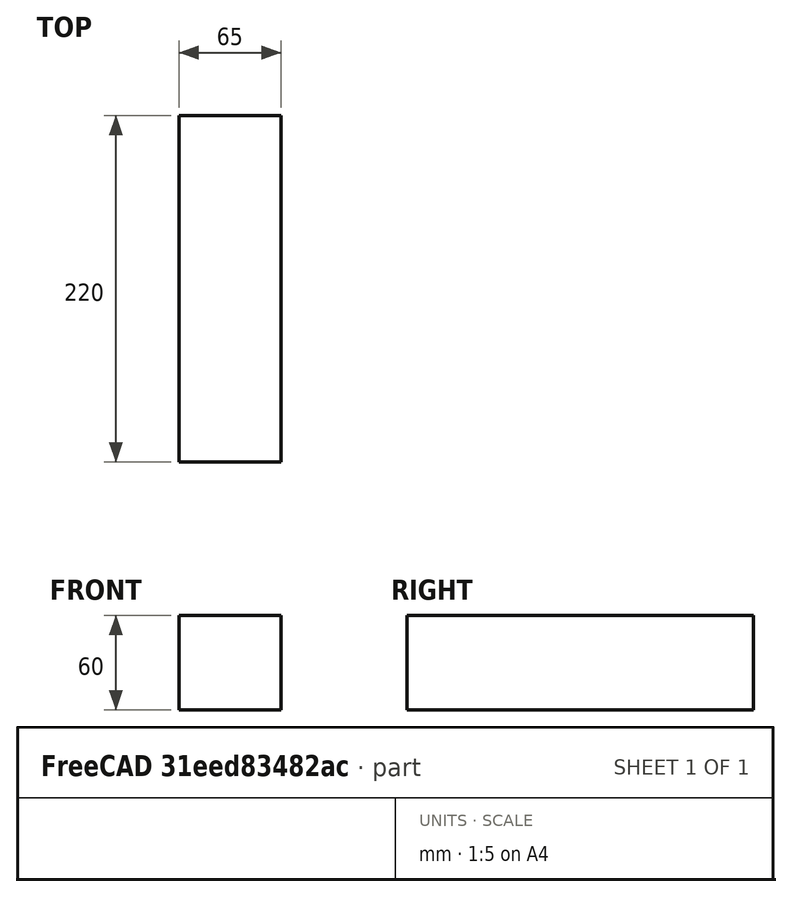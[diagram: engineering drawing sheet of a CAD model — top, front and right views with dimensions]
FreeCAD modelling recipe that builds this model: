
FCSTD DOCUMENT  (FreeCAD 0.15R4669 (Git))
Label: BR_batterie
License: All rights reserved
LicenseURL: http://en.wikipedia.org/wiki/All_rights_reserved
objects: Sketcher::SketchObject×1, Part::Extrusion×1
note: 2 computed .brp shape members not serialized (recipe doc carries the construction recipe); baked Part::Feature solids carry a one-line shape summary decoded from their .brp

FEATURE [Sketcher::SketchObject] Sketch  label="coupeBatt"
  Placement = pos=(0,0,0) rot=(-1,0,0;4.71239rad)
  sketch-geometry (4):
    g0: LineSegment StartX=-32.5 StartY=30 StartZ=0 EndX=32.5 EndY=30 EndZ=0
    g1: LineSegment StartX=32.5 StartY=30 StartZ=0 EndX=32.5 EndY=-30 EndZ=0
    g2: LineSegment StartX=32.5 StartY=-30 StartZ=0 EndX=-32.5 EndY=-30 EndZ=0
    g3: LineSegment StartX=-32.5 StartY=-30 StartZ=0 EndX=-32.5 EndY=30 EndZ=0
  constraints (12):
    c: Coincident(g0,g1)
    c: Coincident(g1,g2)
    c: Coincident(g2,g3)
    c: Coincident(g3,g0)
    c: Horizontal(g0)
    c: Horizontal(g2)
    c: Vertical(g1)
    c: Vertical(g3)
    c: Symmetric(g0,g0,g-2)
    c: Symmetric(g0,g2,g-1)
    c: DistanceX(g0) = 65
    c: DistanceY(g1) = -60
FEATURE [Part::Extrusion] Extrude001  label="batterie"
  Base = -> Sketch
  Dir = (0,220,0)
  Solid = true
